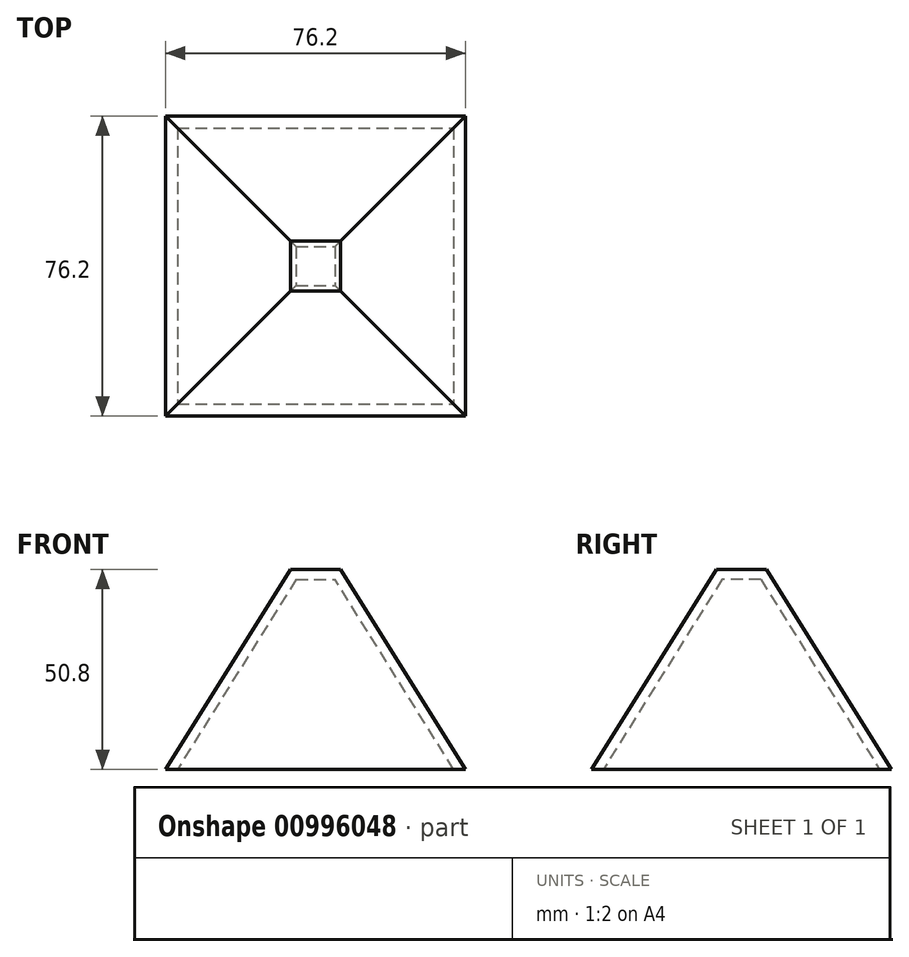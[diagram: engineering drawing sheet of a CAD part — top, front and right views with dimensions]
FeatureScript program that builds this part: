
annotation { "Feature Type Name" : "Feature", "Feature Type Description" : "" }
export const myFeature = defineFeature(function(context is Context, id is Id, definition is map)
    precondition{}
    {
        {
            var Q0;
            Q0=qCreatedBy(makeId("Top.planeOp"),FACE);
            var sketch = newSketch(context, id + "F0", { "sketchPlane" : qUnion([Q0])});
            skLineSegment(sketch, "E0.bottom", {"start": v(-38.1, 38.1) * mm, "end": v(38.1, 38.1) * mm});
            skLineSegment(sketch, "E0.top", {"start": v(-38.1, -38.1) * mm, "end": v(38.1, -38.1) * mm});
            skLineSegment(sketch, "E0.left", {"start": v(-38.1, 38.1) * mm, "end": v(-38.1, -38.1) * mm});
            skLineSegment(sketch, "E0.right", {"start": v(38.1, 38.1) * mm, "end": v(38.1, -38.1) * mm});
            skSolve(sketch);
        }
        {
            var Q0;
            Q0=qCreatedBy(makeId("Top.planeOp"),FACE);
            cPlane(context, id + "F1", {"entities" : qUnion([Q0]), "cplaneType" : CPlaneType.OFFSET, "offset" : 50.8 * mm, "width" : 152.4 * mm, "height" : 152.4 * mm});
        }
        {
            var Q0;
            Q0=qCreatedBy(id+"F1.planeOp",FACE);
            var sketch = newSketch(context, id + "F2", { "sketchPlane" : qUnion([Q0])});
            skLineSegment(sketch, "E1.bottom", {"start": v(-6.35, 6.35) * mm, "end": v(6.35, 6.35) * mm});
            skLineSegment(sketch, "E1.top", {"start": v(-6.35, -6.35) * mm, "end": v(6.35, -6.35) * mm});
            skLineSegment(sketch, "E1.left", {"start": v(-6.35, 6.35) * mm, "end": v(-6.35, -6.35) * mm});
            skLineSegment(sketch, "E1.right", {"start": v(6.35, 6.35) * mm, "end": v(6.35, -6.35) * mm});
            skSolve(sketch);
        }
        {
            var Q0;
            Q0=makeQuery(id+"F0.imprint","IMPRINT",FACE,{"disambiguationData":[TD([[makeQuery(id+"F0.imprint","IMPRINT",EDGE,{"derivedFrom":sQuery(id+"F0.wireOp",EDGE,"E0.bottom")}),-1.0]])]});
            var Q1;
            Q1=makeQuery(id+"F2.imprint","IMPRINT",FACE,{"disambiguationData":[TD([[makeQuery(id+"F2.imprint","IMPRINT",EDGE,{"derivedFrom":sQuery(id+"F2.wireOp",EDGE,"E1.bottom")}),-1.0]])]});
            loft(context, id + "F3", {"sheetProfilesArray" : [{ "sheetProfileEntities" : qUnion([Q0]) }, { "sheetProfileEntities" : qUnion([Q1]) }]});
        }
        {
            var Q0;
            Q0=makeQuery(id+"F3.opLoft","CAP_FACE",FACE,{"disambiguationData":[OSD([makeQuery(id+"F0.imprint","IMPRINT",FACE,{"disambiguationData":[TD([[makeQuery(id+"F0.imprint","IMPRINT",EDGE,{"derivedFrom":sQuery(id+"F0.wireOp",EDGE,"E0.bottom")}),-1.0]])]})])],"isStart":true});
            shell(context, id + "F4", {"entities" : qUnion([Q0]), "thickness" : 2.54 * mm});
        }
    });
